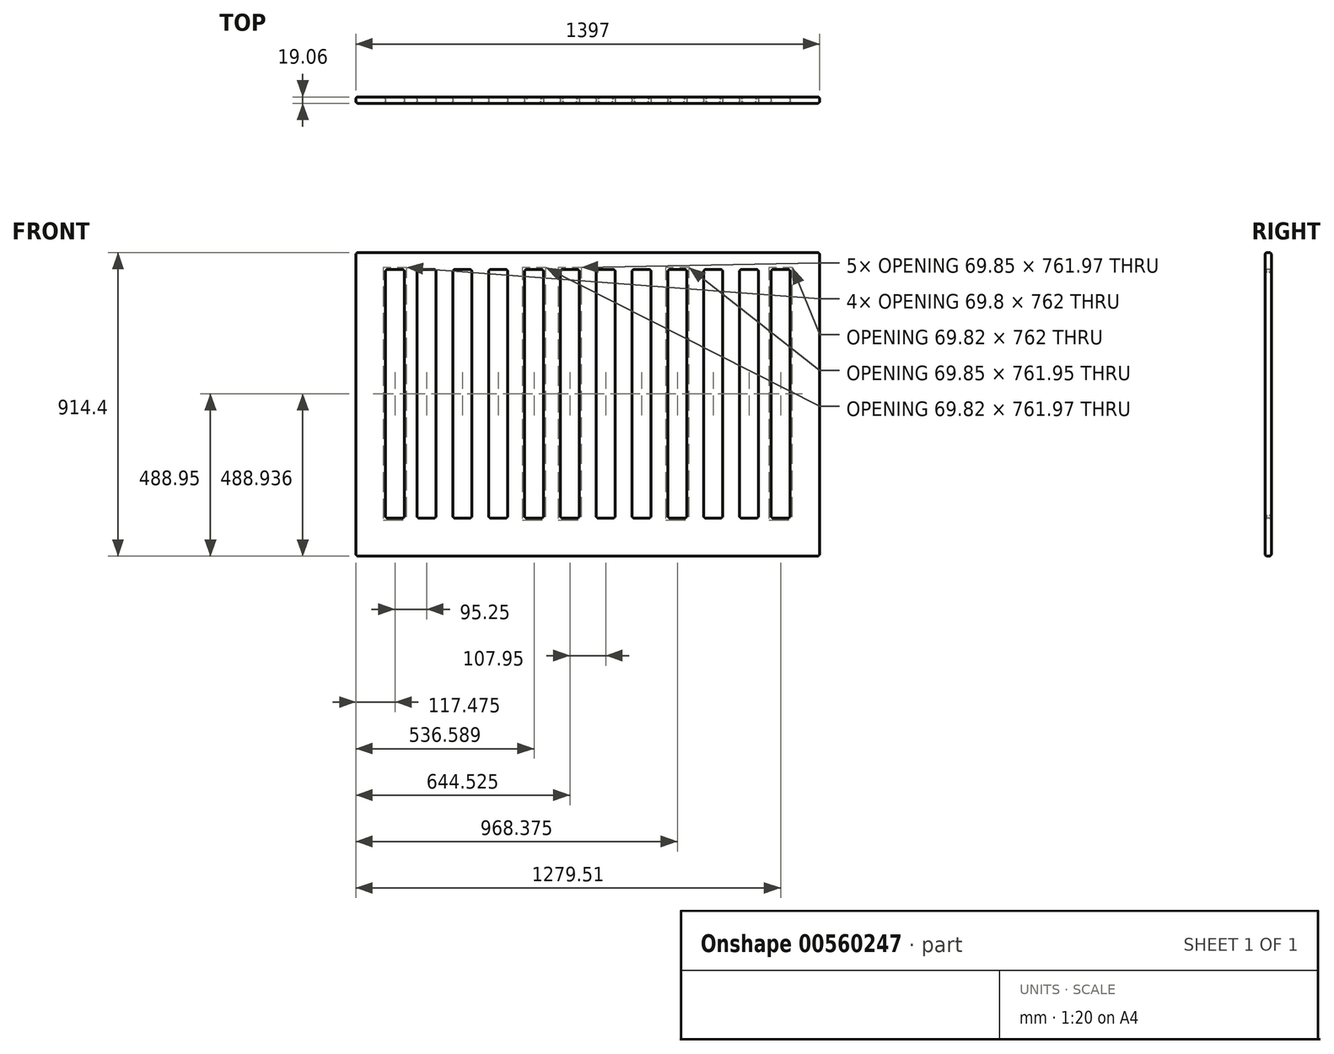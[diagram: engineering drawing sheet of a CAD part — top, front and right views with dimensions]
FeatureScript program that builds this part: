
annotation { "Feature Type Name" : "Feature", "Feature Type Description" : "" }
export const myFeature = defineFeature(function(context is Context, id is Id, definition is map)
    precondition{}
    {
        {
            var Q0;
            Q0=qCreatedBy(makeId("Front.planeOp"),FACE);
            var sketch = newSketch(context, id + "F0", { "sketchPlane" : qUnion([Q0])});
            skLineSegment(sketch, "E0.bottom", {"start": v(-698.5, 457.2) * mm, "end": v(698.5, 457.2) * mm});
            skLineSegment(sketch, "E0.top", {"start": v(-698.5, -457.2) * mm, "end": v(698.5, -457.2) * mm});
            skLineSegment(sketch, "E0.left", {"start": v(-698.5, 457.2) * mm, "end": v(-698.5, -457.2) * mm});
            skLineSegment(sketch, "E0.right", {"start": v(698.5, 457.2) * mm, "end": v(698.5, -457.2) * mm});
            skSolve(sketch);
        }
        {
            var Q0;
            Q0 = qSketchRegion(id + "F0", true);
            extrude(context, id + "F1", {"entities" : qUnion([Q0]), "endBound" : BoundingType.SYMMETRIC, "depth" : 19.05 * mm, "offsetDistance" : 25.4 * mm});
        }
        {
            var Q0;
            Q0=makeQuery(id+"F1.opExtrude","CAP_FACE",FACE,{"disambiguationData":[OSD([sQuery(id+"F0.wireOp",EDGE,"E0.bottom"),sQuery(id+"F0.wireOp",EDGE,"E0.top"),sQuery(id+"F0.wireOp",EDGE,"E0.left"),sQuery(id+"F0.wireOp",EDGE,"E0.right")])],"isStart":false});
            var sketch = newSketch(context, id + "F2", { "sketchPlane" : qUnion([Q0])});
            skLineSegment(sketch, "E1.bottom", {"start": v(-609.6, 406.4) * mm, "end": v(-552.45, 406.4) * mm});
            skLineSegment(sketch, "E1.top", {"start": v(-609.6, -342.9) * mm, "end": v(-552.45, -342.9) * mm});
            skLineSegment(sketch, "E1.left", {"start": v(-609.6, 406.4) * mm, "end": v(-609.6, -342.9) * mm});
            skLineSegment(sketch, "E1.right", {"start": v(-552.45, 406.4) * mm, "end": v(-552.45, -342.9) * mm});
            skLineSegment(sketch, "E2", {"start": v(0, 457.2) * mm, "end": v(0, -457.2) * mm, "construction": true});
            skLineSegment(sketch, "E3.bottom", {"start": v(-25.4, 406.4) * mm, "end": v(-82.55, 406.4) * mm});
            skLineSegment(sketch, "E3.top", {"start": v(-25.4, -342.9) * mm, "end": v(-82.55, -342.9) * mm});
            skLineSegment(sketch, "E3.left", {"start": v(-25.4, 406.4) * mm, "end": v(-25.4, -342.9) * mm});
            skLineSegment(sketch, "E3.right", {"start": v(-82.55, 406.4) * mm, "end": v(-82.55, -342.9) * mm});
            skLineSegment(sketch, "E4.bottom", {"start": v(-133.35, 406.4) * mm, "end": v(-190.5, 406.4) * mm});
            skLineSegment(sketch, "E4.top", {"start": v(-133.35, -342.9) * mm, "end": v(-190.5, -342.9) * mm});
            skLineSegment(sketch, "E4.left", {"start": v(-133.35, 406.4) * mm, "end": v(-133.35, -342.9) * mm});
            skLineSegment(sketch, "E4.right", {"start": v(-190.5, 406.4) * mm, "end": v(-190.5, -342.9) * mm});
            skLineSegment(sketch, "E5.bottom", {"start": v(-241.3, 406.4) * mm, "end": v(-298.45, 406.4) * mm});
            skLineSegment(sketch, "E5.top", {"start": v(-241.3, -342.9) * mm, "end": v(-298.45, -342.9) * mm});
            skLineSegment(sketch, "E5.left", {"start": v(-241.3, 406.4) * mm, "end": v(-241.3, -342.9) * mm});
            skLineSegment(sketch, "E5.right", {"start": v(-298.45, 406.4) * mm, "end": v(-298.45, -342.9) * mm});
            skLineSegment(sketch, "E6.bottom", {"start": v(-349.25, 406.4) * mm, "end": v(-406.4, 406.4) * mm});
            skLineSegment(sketch, "E6.top", {"start": v(-349.25, -342.9) * mm, "end": v(-406.4, -342.9) * mm});
            skLineSegment(sketch, "E6.left", {"start": v(-349.25, 406.4) * mm, "end": v(-349.25, -342.9) * mm});
            skLineSegment(sketch, "E6.right", {"start": v(-406.4, 406.4) * mm, "end": v(-406.4, -342.9) * mm});
            skLineSegment(sketch, "E7.bottom", {"start": v(-457.2, 406.4) * mm, "end": v(-514.35, 406.4) * mm});
            skLineSegment(sketch, "E7.top", {"start": v(-457.2, -342.9) * mm, "end": v(-514.35, -342.9) * mm});
            skLineSegment(sketch, "E7.left", {"start": v(-457.2, 406.4) * mm, "end": v(-457.2, -342.9) * mm});
            skLineSegment(sketch, "E7.right", {"start": v(-514.35, 406.4) * mm, "end": v(-514.35, -342.9) * mm});
            skLineSegment(sketch, "E8.MirrorCS", {"start": v(25.4, 406.4) * mm, "end": v(25.4, -342.9) * mm});
            skLineSegment(sketch, "E9.MirrorCS", {"start": v(25.4, 406.4) * mm, "end": v(82.55, 406.4) * mm});
            skLineSegment(sketch, "E10.MirrorCS", {"start": v(82.55, 406.4) * mm, "end": v(82.55, -342.9) * mm});
            skLineSegment(sketch, "E11.MirrorCS", {"start": v(25.4, -342.9) * mm, "end": v(82.55, -342.9) * mm});
            skLineSegment(sketch, "E12.MirrorCS", {"start": v(133.35, -342.9) * mm, "end": v(190.5, -342.9) * mm});
            skLineSegment(sketch, "E13.MirrorCS", {"start": v(241.3, -342.9) * mm, "end": v(298.45, -342.9) * mm});
            skLineSegment(sketch, "E14.MirrorCS", {"start": v(349.25, -342.9) * mm, "end": v(406.4, -342.9) * mm});
            skLineSegment(sketch, "E15.MirrorCS", {"start": v(457.2, -342.9) * mm, "end": v(514.35, -342.9) * mm});
            skLineSegment(sketch, "E16.MirrorCS", {"start": v(609.6, -342.9) * mm, "end": v(552.45, -342.9) * mm});
            skLineSegment(sketch, "E17.MirrorCS", {"start": v(609.6, 406.4) * mm, "end": v(552.45, 406.4) * mm});
            skLineSegment(sketch, "E18.MirrorCS", {"start": v(349.25, 406.4) * mm, "end": v(406.4, 406.4) * mm});
            skLineSegment(sketch, "E19.MirrorCS", {"start": v(457.2, 406.4) * mm, "end": v(514.35, 406.4) * mm});
            skLineSegment(sketch, "E20.MirrorCS", {"start": v(241.3, 406.4) * mm, "end": v(298.45, 406.4) * mm});
            skLineSegment(sketch, "E21.MirrorCS", {"start": v(133.35, 406.4) * mm, "end": v(190.5, 406.4) * mm});
            skLineSegment(sketch, "E22.MirrorCS", {"start": v(133.35, 406.4) * mm, "end": v(133.35, -342.9) * mm});
            skLineSegment(sketch, "E23.MirrorCS", {"start": v(190.5, 406.4) * mm, "end": v(190.5, -342.9) * mm});
            skLineSegment(sketch, "E24.MirrorCS", {"start": v(241.3, 406.4) * mm, "end": v(241.3, -342.9) * mm});
            skLineSegment(sketch, "E25.MirrorCS", {"start": v(298.45, 406.4) * mm, "end": v(298.45, -342.9) * mm});
            skLineSegment(sketch, "E26.MirrorCS", {"start": v(349.25, 406.4) * mm, "end": v(349.25, -342.9) * mm});
            skLineSegment(sketch, "E27.MirrorCS", {"start": v(406.4, 406.4) * mm, "end": v(406.4, -342.9) * mm});
            skLineSegment(sketch, "E28.MirrorCS", {"start": v(457.2, 406.4) * mm, "end": v(457.2, -342.9) * mm});
            skLineSegment(sketch, "E29.MirrorCS", {"start": v(514.35, 406.4) * mm, "end": v(514.35, -342.9) * mm});
            skLineSegment(sketch, "E30.MirrorCS", {"start": v(552.45, 406.4) * mm, "end": v(552.45, -342.9) * mm});
            skLineSegment(sketch, "E31.MirrorCS", {"start": v(609.6, 406.4) * mm, "end": v(609.6, -342.9) * mm});
            skSolve(sketch);
        }
        {
            var Q0;
            Q0=makeQuery(id+"F2.imprint","IMPRINT",FACE,{"disambiguationData":[TD([[makeQuery(id+"F2.imprint","IMPRINT",EDGE,{"derivedFrom":sQuery(id+"F2.wireOp",EDGE,"E1.bottom")}),-1.0]])]});
            var Q1;
            Q1=makeQuery(id+"F2.imprint","IMPRINT",FACE,{"disambiguationData":[TD([[makeQuery(id+"F2.imprint","IMPRINT",EDGE,{"derivedFrom":sQuery(id+"F2.wireOp",EDGE,"E7.bottom")}),1.0]])]});
            var Q2;
            Q2=makeQuery(id+"F2.imprint","IMPRINT",FACE,{"disambiguationData":[TD([[makeQuery(id+"F2.imprint","IMPRINT",EDGE,{"derivedFrom":sQuery(id+"F2.wireOp",EDGE,"E6.bottom")}),1.0]])]});
            var Q3;
            Q3=makeQuery(id+"F2.imprint","IMPRINT",FACE,{"disambiguationData":[TD([[makeQuery(id+"F2.imprint","IMPRINT",EDGE,{"derivedFrom":sQuery(id+"F2.wireOp",EDGE,"E5.bottom")}),1.0]])]});
            var Q4;
            Q4=makeQuery(id+"F2.imprint","IMPRINT",FACE,{"disambiguationData":[TD([[makeQuery(id+"F2.imprint","IMPRINT",EDGE,{"derivedFrom":sQuery(id+"F2.wireOp",EDGE,"E4.bottom")}),1.0]])]});
            var Q5;
            Q5=makeQuery(id+"F2.imprint","IMPRINT",FACE,{"disambiguationData":[TD([[makeQuery(id+"F2.imprint","IMPRINT",EDGE,{"derivedFrom":sQuery(id+"F2.wireOp",EDGE,"E3.bottom")}),1.0]])]});
            var Q6;
            Q6=makeQuery(id+"F2.imprint","IMPRINT",FACE,{"disambiguationData":[TD([[makeQuery(id+"F2.imprint","IMPRINT",EDGE,{"derivedFrom":sQuery(id+"F2.wireOp",EDGE,"E8.MirrorCS")}),1.0]])]});
            var Q7;
            Q7=makeQuery(id+"F2.imprint","IMPRINT",FACE,{"disambiguationData":[TD([[makeQuery(id+"F2.imprint","IMPRINT",EDGE,{"derivedFrom":sQuery(id+"F2.wireOp",EDGE,"E12.MirrorCS")}),1.0]])]});
            var Q8;
            Q8=makeQuery(id+"F2.imprint","IMPRINT",FACE,{"disambiguationData":[TD([[makeQuery(id+"F2.imprint","IMPRINT",EDGE,{"derivedFrom":sQuery(id+"F2.wireOp",EDGE,"E13.MirrorCS")}),1.0]])]});
            var Q9;
            Q9=makeQuery(id+"F2.imprint","IMPRINT",FACE,{"disambiguationData":[TD([[makeQuery(id+"F2.imprint","IMPRINT",EDGE,{"derivedFrom":sQuery(id+"F2.wireOp",EDGE,"E14.MirrorCS")}),1.0]])]});
            var Q10;
            Q10=makeQuery(id+"F2.imprint","IMPRINT",FACE,{"disambiguationData":[TD([[makeQuery(id+"F2.imprint","IMPRINT",EDGE,{"derivedFrom":sQuery(id+"F2.wireOp",EDGE,"E15.MirrorCS")}),1.0]])]});
            var Q11;
            Q11=makeQuery(id+"F2.imprint","IMPRINT",FACE,{"disambiguationData":[TD([[makeQuery(id+"F2.imprint","IMPRINT",EDGE,{"derivedFrom":sQuery(id+"F2.wireOp",EDGE,"E16.MirrorCS")}),-1.0]])]});
            extrude(context, id + "F3", {"entities" : qUnion([Q0, Q1, Q2, Q3, Q4, Q5, Q6, Q7, Q8, Q9, Q10, Q11]), "operationType" : NewBodyOperationType.REMOVE, "endBound" : BoundingType.THROUGH_ALL, "oppositeDirection" : true, "depth" : 25.4 * mm, "offsetDistance" : 25.4 * mm});
        }
        {
            var Q0;
            Q0=makeQuery(id+"F3.boolean.opBoolean","COPY",EDGE,{"derivedFrom":makeQuery(id+"F3.opExtrude","CAP_EDGE",EDGE,{"disambiguationData":[OSD([sQuery(id+"F2.wireOp",EDGE,"E1.left")])],"isStart":true})});
            var Q1;
            Q1=makeQuery(id+"F3.boolean.opBoolean","INTERSECT",EDGE,{"derivedFrom":[makeQuery(id+"F1.opExtrude","CAP_FACE",FACE,{"disambiguationData":[OSD([sQuery(id+"F0.wireOp",EDGE,"E0.bottom"),sQuery(id+"F0.wireOp",EDGE,"E0.top"),sQuery(id+"F0.wireOp",EDGE,"E0.left"),sQuery(id+"F0.wireOp",EDGE,"E0.right")])],"isStart":true}),makeQuery(id+"F3.opExtrude","SWEPT_FACE",FACE,{"disambiguationData":[OSD([sQuery(id+"F2.wireOp",EDGE,"E1.left")])]})]});
            var Q2;
            Q2=makeQuery(id+"F3.boolean.opBoolean","COPY",EDGE,{"derivedFrom":makeQuery(id+"F3.opExtrude","CAP_EDGE",EDGE,{"disambiguationData":[OSD([sQuery(id+"F2.wireOp",EDGE,"E1.right")])],"isStart":true})});
            var Q3;
            Q3=makeQuery(id+"F3.boolean.opBoolean","COPY",EDGE,{"derivedFrom":makeQuery(id+"F3.opExtrude","CAP_EDGE",EDGE,{"disambiguationData":[OSD([sQuery(id+"F2.wireOp",EDGE,"E7.right")])],"isStart":true})});
            var Q4;
            Q4=makeQuery(id+"F3.boolean.opBoolean","INTERSECT",EDGE,{"derivedFrom":[makeQuery(id+"F1.opExtrude","CAP_FACE",FACE,{"disambiguationData":[OSD([sQuery(id+"F0.wireOp",EDGE,"E0.bottom"),sQuery(id+"F0.wireOp",EDGE,"E0.top"),sQuery(id+"F0.wireOp",EDGE,"E0.left"),sQuery(id+"F0.wireOp",EDGE,"E0.right")])],"isStart":true}),makeQuery(id+"F3.opExtrude","SWEPT_FACE",FACE,{"disambiguationData":[OSD([sQuery(id+"F2.wireOp",EDGE,"E7.right")])]})]});
            var Q5;
            Q5=makeQuery(id+"F3.boolean.opBoolean","COPY",EDGE,{"derivedFrom":makeQuery(id+"F3.opExtrude","CAP_EDGE",EDGE,{"disambiguationData":[OSD([sQuery(id+"F2.wireOp",EDGE,"E7.left")])],"isStart":true})});
            var Q6;
            Q6=makeQuery(id+"F3.boolean.opBoolean","COPY",EDGE,{"derivedFrom":makeQuery(id+"F3.opExtrude","CAP_EDGE",EDGE,{"disambiguationData":[OSD([sQuery(id+"F2.wireOp",EDGE,"E6.right")])],"isStart":true})});
            var Q7;
            Q7=makeQuery(id+"F3.boolean.opBoolean","INTERSECT",EDGE,{"derivedFrom":[makeQuery(id+"F1.opExtrude","CAP_FACE",FACE,{"disambiguationData":[OSD([sQuery(id+"F0.wireOp",EDGE,"E0.bottom"),sQuery(id+"F0.wireOp",EDGE,"E0.top"),sQuery(id+"F0.wireOp",EDGE,"E0.left"),sQuery(id+"F0.wireOp",EDGE,"E0.right")])],"isStart":true}),makeQuery(id+"F3.opExtrude","SWEPT_FACE",FACE,{"disambiguationData":[OSD([sQuery(id+"F2.wireOp",EDGE,"E6.right")])]})]});
            var Q8;
            Q8=makeQuery(id+"F3.boolean.opBoolean","COPY",EDGE,{"derivedFrom":makeQuery(id+"F3.opExtrude","CAP_EDGE",EDGE,{"disambiguationData":[OSD([sQuery(id+"F2.wireOp",EDGE,"E6.left")])],"isStart":true})});
            var Q9;
            Q9=makeQuery(id+"F3.boolean.opBoolean","COPY",EDGE,{"derivedFrom":makeQuery(id+"F3.opExtrude","CAP_EDGE",EDGE,{"disambiguationData":[OSD([sQuery(id+"F2.wireOp",EDGE,"E5.right")])],"isStart":true})});
            var Q10;
            Q10=makeQuery(id+"F3.boolean.opBoolean","INTERSECT",EDGE,{"derivedFrom":[makeQuery(id+"F1.opExtrude","CAP_FACE",FACE,{"disambiguationData":[OSD([sQuery(id+"F0.wireOp",EDGE,"E0.bottom"),sQuery(id+"F0.wireOp",EDGE,"E0.top"),sQuery(id+"F0.wireOp",EDGE,"E0.left"),sQuery(id+"F0.wireOp",EDGE,"E0.right")])],"isStart":true}),makeQuery(id+"F3.opExtrude","SWEPT_FACE",FACE,{"disambiguationData":[OSD([sQuery(id+"F2.wireOp",EDGE,"E5.right")])]})]});
            var Q11;
            Q11=makeQuery(id+"F3.boolean.opBoolean","COPY",EDGE,{"derivedFrom":makeQuery(id+"F3.opExtrude","CAP_EDGE",EDGE,{"disambiguationData":[OSD([sQuery(id+"F2.wireOp",EDGE,"E5.left")])],"isStart":true})});
            var Q12;
            Q12=makeQuery(id+"F3.boolean.opBoolean","COPY",EDGE,{"derivedFrom":makeQuery(id+"F3.opExtrude","CAP_EDGE",EDGE,{"disambiguationData":[OSD([sQuery(id+"F2.wireOp",EDGE,"E5.bottom")])],"isStart":true})});
            var Q13;
            Q13=makeQuery(id+"F3.boolean.opBoolean","COPY",EDGE,{"derivedFrom":makeQuery(id+"F3.opExtrude","CAP_EDGE",EDGE,{"disambiguationData":[OSD([sQuery(id+"F2.wireOp",EDGE,"E6.bottom")])],"isStart":true})});
            var Q14;
            Q14=makeQuery(id+"F3.boolean.opBoolean","COPY",EDGE,{"derivedFrom":makeQuery(id+"F3.opExtrude","CAP_EDGE",EDGE,{"disambiguationData":[OSD([sQuery(id+"F2.wireOp",EDGE,"E7.bottom")])],"isStart":true})});
            var Q15;
            Q15=makeQuery(id+"F3.boolean.opBoolean","COPY",EDGE,{"derivedFrom":makeQuery(id+"F3.opExtrude","CAP_EDGE",EDGE,{"disambiguationData":[OSD([sQuery(id+"F2.wireOp",EDGE,"E1.bottom")])],"isStart":true})});
            var Q16;
            Q16=makeQuery(id+"F1.opExtrude","CAP_EDGE",EDGE,{"disambiguationData":[OSD([sQuery(id+"F0.wireOp",EDGE,"E0.left")])],"isStart":false});
            var Q17;
            Q17=makeQuery(id+"F1.opExtrude","CAP_EDGE",EDGE,{"disambiguationData":[OSD([sQuery(id+"F0.wireOp",EDGE,"E0.bottom")])],"isStart":false});
            var Q18;
            Q18=makeQuery(id+"F1.opExtrude","CAP_EDGE",EDGE,{"disambiguationData":[OSD([sQuery(id+"F0.wireOp",EDGE,"E0.bottom")])],"isStart":true});
            var Q19;
            Q19=makeQuery(id+"F3.boolean.opBoolean","COPY",EDGE,{"derivedFrom":makeQuery(id+"F3.opExtrude","CAP_EDGE",EDGE,{"disambiguationData":[OSD([sQuery(id+"F2.wireOp",EDGE,"E4.bottom")])],"isStart":true})});
            var Q20;
            Q20=makeQuery(id+"F3.boolean.opBoolean","COPY",EDGE,{"derivedFrom":makeQuery(id+"F3.opExtrude","CAP_EDGE",EDGE,{"disambiguationData":[OSD([sQuery(id+"F2.wireOp",EDGE,"E4.right")])],"isStart":true})});
            var Q21;
            Q21=makeQuery(id+"F3.boolean.opBoolean","INTERSECT",EDGE,{"derivedFrom":[makeQuery(id+"F1.opExtrude","CAP_FACE",FACE,{"disambiguationData":[OSD([sQuery(id+"F0.wireOp",EDGE,"E0.bottom"),sQuery(id+"F0.wireOp",EDGE,"E0.top"),sQuery(id+"F0.wireOp",EDGE,"E0.left"),sQuery(id+"F0.wireOp",EDGE,"E0.right")])],"isStart":true}),makeQuery(id+"F3.opExtrude","SWEPT_FACE",FACE,{"disambiguationData":[OSD([sQuery(id+"F2.wireOp",EDGE,"E4.right")])]})]});
            var Q22;
            Q22=makeQuery(id+"F3.boolean.opBoolean","COPY",EDGE,{"derivedFrom":makeQuery(id+"F3.opExtrude","CAP_EDGE",EDGE,{"disambiguationData":[OSD([sQuery(id+"F2.wireOp",EDGE,"E4.left")])],"isStart":true})});
            var Q23;
            Q23=makeQuery(id+"F3.boolean.opBoolean","COPY",FACE,{"derivedFrom":makeQuery(id+"F3.opExtrude","SWEPT_FACE",FACE,{"disambiguationData":[OSD([sQuery(id+"F2.wireOp",EDGE,"E3.right")])]})});
            var Q24;
            Q24=makeQuery(id+"F3.boolean.opBoolean","COPY",FACE,{"derivedFrom":makeQuery(id+"F3.opExtrude","SWEPT_FACE",FACE,{"disambiguationData":[OSD([sQuery(id+"F2.wireOp",EDGE,"E8.MirrorCS")])]})});
            var Q25;
            Q25=makeQuery(id+"F3.boolean.opBoolean","COPY",EDGE,{"derivedFrom":makeQuery(id+"F3.opExtrude","CAP_EDGE",EDGE,{"disambiguationData":[OSD([sQuery(id+"F2.wireOp",EDGE,"E3.left")])],"isStart":true})});
            var Q26;
            Q26=makeQuery(id+"F3.boolean.opBoolean","COPY",EDGE,{"derivedFrom":makeQuery(id+"F3.opExtrude","CAP_EDGE",EDGE,{"disambiguationData":[OSD([sQuery(id+"F2.wireOp",EDGE,"E10.MirrorCS")])],"isStart":true})});
            var Q27;
            Q27=makeQuery(id+"F3.boolean.opBoolean","COPY",FACE,{"derivedFrom":makeQuery(id+"F3.opExtrude","SWEPT_FACE",FACE,{"disambiguationData":[OSD([sQuery(id+"F2.wireOp",EDGE,"E22.MirrorCS")])]})});
            var Q28;
            Q28=makeQuery(id+"F3.boolean.opBoolean","COPY",FACE,{"derivedFrom":makeQuery(id+"F3.opExtrude","SWEPT_FACE",FACE,{"disambiguationData":[OSD([sQuery(id+"F2.wireOp",EDGE,"E24.MirrorCS")])]})});
            var Q29;
            Q29=makeQuery(id+"F3.boolean.opBoolean","COPY",EDGE,{"derivedFrom":makeQuery(id+"F3.opExtrude","CAP_EDGE",EDGE,{"disambiguationData":[OSD([sQuery(id+"F2.wireOp",EDGE,"E23.MirrorCS")])],"isStart":true})});
            var Q30;
            Q30=makeQuery(id+"F3.boolean.opBoolean","COPY",EDGE,{"derivedFrom":makeQuery(id+"F3.opExtrude","CAP_EDGE",EDGE,{"disambiguationData":[OSD([sQuery(id+"F2.wireOp",EDGE,"E25.MirrorCS")])],"isStart":true})});
            var Q31;
            Q31=makeQuery(id+"F3.boolean.opBoolean","COPY",FACE,{"derivedFrom":makeQuery(id+"F3.opExtrude","SWEPT_FACE",FACE,{"disambiguationData":[OSD([sQuery(id+"F2.wireOp",EDGE,"E26.MirrorCS")])]})});
            var Q32;
            Q32=makeQuery(id+"F3.boolean.opBoolean","COPY",EDGE,{"derivedFrom":makeQuery(id+"F3.opExtrude","SWEPT_EDGE",EDGE,{"disambiguationData":[OSD([sQuery(id+"F2.wireOp",EDGE,"E4.bottom"),sQuery(id+"F2.wireOp",EDGE,"E4.right")])]})});
            var Q33;
            Q33=makeQuery(id+"F3.boolean.opBoolean","COPY",FACE,{"derivedFrom":makeQuery(id+"F3.opExtrude","SWEPT_FACE",FACE,{"disambiguationData":[OSD([sQuery(id+"F2.wireOp",EDGE,"E5.bottom")])]})});
            var Q34;
            Q34=makeQuery(id+"F3.boolean.opBoolean","COPY",FACE,{"derivedFrom":makeQuery(id+"F3.opExtrude","SWEPT_FACE",FACE,{"disambiguationData":[OSD([sQuery(id+"F2.wireOp",EDGE,"E6.bottom")])]})});
            var Q35;
            Q35=makeQuery(id+"F3.boolean.opBoolean","COPY",FACE,{"derivedFrom":makeQuery(id+"F3.opExtrude","SWEPT_FACE",FACE,{"disambiguationData":[OSD([sQuery(id+"F2.wireOp",EDGE,"E7.bottom")])]})});
            var Q36;
            Q36=makeQuery(id+"F3.boolean.opBoolean","COPY",FACE,{"derivedFrom":makeQuery(id+"F3.opExtrude","SWEPT_FACE",FACE,{"disambiguationData":[OSD([sQuery(id+"F2.wireOp",EDGE,"E1.bottom")])]})});
            var Q37;
            Q37=makeQuery(id+"F3.boolean.opBoolean","COPY",FACE,{"derivedFrom":makeQuery(id+"F3.opExtrude","SWEPT_FACE",FACE,{"disambiguationData":[OSD([sQuery(id+"F2.wireOp",EDGE,"E28.MirrorCS")])]})});
            var Q38;
            Q38=makeQuery(id+"F3.boolean.opBoolean","COPY",FACE,{"derivedFrom":makeQuery(id+"F3.opExtrude","SWEPT_FACE",FACE,{"disambiguationData":[OSD([sQuery(id+"F2.wireOp",EDGE,"E30.MirrorCS")])]})});
            var Q39;
            Q39=makeQuery(id+"F1.opExtrude","SWEPT_FACE",FACE,{"disambiguationData":[OSD([sQuery(id+"F0.wireOp",EDGE,"E0.right")])]});
            var Q40;
            Q40=makeQuery(id+"F1.opExtrude","SWEPT_EDGE",EDGE,{"disambiguationData":[OSD([sQuery(id+"F0.wireOp",EDGE,"E0.bottom"),sQuery(id+"F0.wireOp",EDGE,"E0.left")])]});
            var Q41;
            Q41=makeQuery(id+"F1.opExtrude","SWEPT_FACE",FACE,{"disambiguationData":[OSD([sQuery(id+"F0.wireOp",EDGE,"E0.left")])]});
            var Q42;
            Q42=makeQuery(id+"F1.opExtrude","SWEPT_FACE",FACE,{"disambiguationData":[OSD([sQuery(id+"F0.wireOp",EDGE,"E0.top")])]});
            var Q43;
            Q43=makeQuery(id+"F3.boolean.opBoolean","COPY",FACE,{"derivedFrom":makeQuery(id+"F3.opExtrude","SWEPT_FACE",FACE,{"disambiguationData":[OSD([sQuery(id+"F2.wireOp",EDGE,"E1.top")])]})});
            var Q44;
            Q44=makeQuery(id+"F3.boolean.opBoolean","COPY",FACE,{"derivedFrom":makeQuery(id+"F3.opExtrude","SWEPT_FACE",FACE,{"disambiguationData":[OSD([sQuery(id+"F2.wireOp",EDGE,"E7.top")])]})});
            var Q45;
            Q45=makeQuery(id+"F3.boolean.opBoolean","COPY",FACE,{"derivedFrom":makeQuery(id+"F3.opExtrude","SWEPT_FACE",FACE,{"disambiguationData":[OSD([sQuery(id+"F2.wireOp",EDGE,"E6.top")])]})});
            var Q46;
            Q46=makeQuery(id+"F3.boolean.opBoolean","COPY",FACE,{"derivedFrom":makeQuery(id+"F3.opExtrude","SWEPT_FACE",FACE,{"disambiguationData":[OSD([sQuery(id+"F2.wireOp",EDGE,"E5.top")])]})});
            var Q47;
            Q47=makeQuery(id+"F3.boolean.opBoolean","COPY",FACE,{"derivedFrom":makeQuery(id+"F3.opExtrude","SWEPT_FACE",FACE,{"disambiguationData":[OSD([sQuery(id+"F2.wireOp",EDGE,"E4.top")])]})});
            var Q48;
            Q48=makeQuery(id+"F3.boolean.opBoolean","COPY",FACE,{"derivedFrom":makeQuery(id+"F3.opExtrude","SWEPT_FACE",FACE,{"disambiguationData":[OSD([sQuery(id+"F2.wireOp",EDGE,"E3.top")])]})});
            var Q49;
            Q49=makeQuery(id+"F3.boolean.opBoolean","COPY",FACE,{"derivedFrom":makeQuery(id+"F3.opExtrude","SWEPT_FACE",FACE,{"disambiguationData":[OSD([sQuery(id+"F2.wireOp",EDGE,"E11.MirrorCS")])]})});
            var Q50;
            Q50=makeQuery(id+"F3.boolean.opBoolean","COPY",FACE,{"derivedFrom":makeQuery(id+"F3.opExtrude","SWEPT_FACE",FACE,{"disambiguationData":[OSD([sQuery(id+"F2.wireOp",EDGE,"E12.MirrorCS")])]})});
            var Q51;
            Q51=makeQuery(id+"F3.boolean.opBoolean","COPY",FACE,{"derivedFrom":makeQuery(id+"F3.opExtrude","SWEPT_FACE",FACE,{"disambiguationData":[OSD([sQuery(id+"F2.wireOp",EDGE,"E14.MirrorCS")])]})});
            var Q52;
            Q52=makeQuery(id+"F3.boolean.opBoolean","COPY",FACE,{"derivedFrom":makeQuery(id+"F3.opExtrude","SWEPT_FACE",FACE,{"disambiguationData":[OSD([sQuery(id+"F2.wireOp",EDGE,"E15.MirrorCS")])]})});
            var Q53;
            Q53=makeQuery(id+"F3.boolean.opBoolean","COPY",FACE,{"derivedFrom":makeQuery(id+"F3.opExtrude","SWEPT_FACE",FACE,{"disambiguationData":[OSD([sQuery(id+"F2.wireOp",EDGE,"E16.MirrorCS")])]})});
            var Q54;
            Q54=makeQuery(id+"F3.boolean.opBoolean","COPY",FACE,{"derivedFrom":makeQuery(id+"F3.opExtrude","SWEPT_FACE",FACE,{"disambiguationData":[OSD([sQuery(id+"F2.wireOp",EDGE,"E17.MirrorCS")])]})});
            var Q55;
            Q55=makeQuery(id+"F3.boolean.opBoolean","COPY",FACE,{"derivedFrom":makeQuery(id+"F3.opExtrude","SWEPT_FACE",FACE,{"disambiguationData":[OSD([sQuery(id+"F2.wireOp",EDGE,"E29.MirrorCS")])]})});
            var Q56;
            Q56=makeQuery(id+"F3.boolean.opBoolean","COPY",FACE,{"derivedFrom":makeQuery(id+"F3.opExtrude","SWEPT_FACE",FACE,{"disambiguationData":[OSD([sQuery(id+"F2.wireOp",EDGE,"E27.MirrorCS")])]})});
            var Q57;
            Q57=makeQuery(id+"F3.boolean.opBoolean","COPY",FACE,{"derivedFrom":makeQuery(id+"F3.opExtrude","SWEPT_FACE",FACE,{"disambiguationData":[OSD([sQuery(id+"F2.wireOp",EDGE,"E25.MirrorCS")])]})});
            var Q58;
            Q58=makeQuery(id+"F3.boolean.opBoolean","COPY",FACE,{"derivedFrom":makeQuery(id+"F3.opExtrude","SWEPT_FACE",FACE,{"disambiguationData":[OSD([sQuery(id+"F2.wireOp",EDGE,"E23.MirrorCS")])]})});
            var Q59;
            Q59=makeQuery(id+"F3.boolean.opBoolean","COPY",FACE,{"derivedFrom":makeQuery(id+"F3.opExtrude","SWEPT_FACE",FACE,{"disambiguationData":[OSD([sQuery(id+"F2.wireOp",EDGE,"E10.MirrorCS")])]})});
            var Q60;
            Q60=makeQuery(id+"F3.boolean.opBoolean","COPY",FACE,{"derivedFrom":makeQuery(id+"F3.opExtrude","SWEPT_FACE",FACE,{"disambiguationData":[OSD([sQuery(id+"F2.wireOp",EDGE,"E3.left")])]})});
            var Q61;
            Q61=makeQuery(id+"F3.boolean.opBoolean","COPY",FACE,{"derivedFrom":makeQuery(id+"F3.opExtrude","SWEPT_FACE",FACE,{"disambiguationData":[OSD([sQuery(id+"F2.wireOp",EDGE,"E4.left")])]})});
            fillet(context, id + "F4", {"entities" : qUnion([Q0, Q1, Q2, Q3, Q4, Q5, Q6, Q7, Q8, Q9, Q10, Q11, Q12, Q13, Q14, Q15, Q16, Q17, Q18, Q19, Q20, Q21, Q22, Q23, Q24, Q25, Q26, Q27, Q28, Q29, Q30, Q31, Q32, Q33, Q34, Q35, Q36, Q37, Q38, Q39, Q40, Q41, Q42, Q43, Q44, Q45, Q46, Q47, Q48, Q49, Q50, Q51, Q52, Q53, Q54, Q55, Q56, Q57, Q58, Q59, Q60, Q61]), "radius" : 6.35 * mm, "tangentPropagation" : true, "allowEdgeOverflow" : false});
        }
    });
